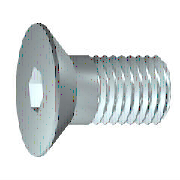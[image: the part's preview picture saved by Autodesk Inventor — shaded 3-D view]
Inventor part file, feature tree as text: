
AUTODESK INVENTOR PART (.ipt)
format: ipt  version: 2020 (Build 240168000, 168)  size: 177,152 bytes
history: native  units: mm (DEFAULTED — no unit token found)
features: sketch x2, extrude x1, plane x1
ambient origin geometry x7: Origin, YZ Plane, XY Plane, X Axis, Y Axis, Z Axis, Center Point
bodies: Solid1 (feature_tree), Body (feature_tree)
feature tree (4):
  sketch  "Sketch2"  dims[d2=1.5mm d3=4.0mm d6=2.48mm d7=45.0deg d8=2.886751mm d9=60.0deg d10=7.53mm d11=4.0mm d12=0.429415mm d13=90.0deg d30=10.0mm d14=0.0mm d15=20.0mm d16=0.0mm d17=0.429415mm d18=0.429415mm d20=0.0mm d39=45.0deg d43=0.0mm d44=0.0mm]
  extrude  "Slot"  Depth=20.0mm
  plane  "Work Plane1"
  sketch  "Sketch1"  dims[d0=35.0mm d1=20.0mm]
